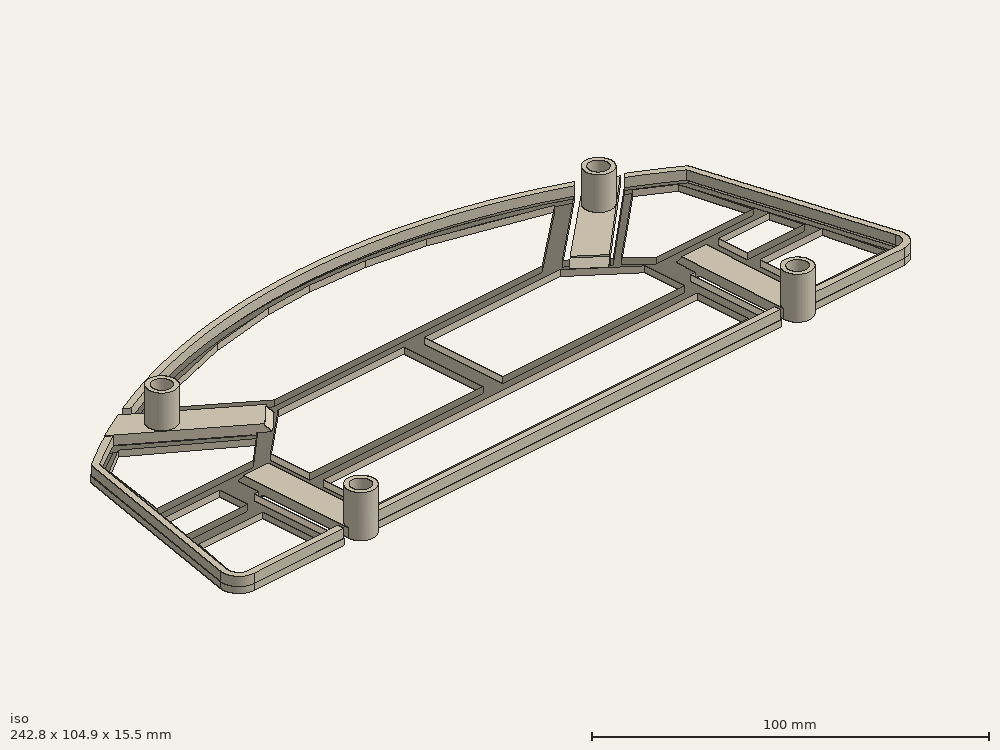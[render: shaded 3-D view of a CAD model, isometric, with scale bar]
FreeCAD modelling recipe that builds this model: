
FCSTD DOCUMENT  (FreeCAD 0.16R6045 (Git))
Label: project_n_rev3
License: All rights reserved
LicenseURL: http://en.wikipedia.org/wiki/All_rights_reserved
objects: Part::Cylinder×8, Sketcher::SketchObject×5, Part::Cut×5, Part::MultiFuse×4, Part::Chamfer×4, PartDesign::Pad×2, Part::Extrusion×2, Part::Thickness×1
note: 33 computed .brp shape members not serialized (recipe doc carries the construction recipe); baked Part::Feature solids carry a one-line shape summary decoded from their .brp

FEATURE [Sketcher::SketchObject] Sketch  label="Base"
  Placement = pos=(0,0,0) rot=(1,0,0;3.14159rad)
  sketch-geometry (71):
    g0: LineSegment StartX=-43.3507 StartY=-6.8712 StartZ=0 EndX=-28.7131 EndY=-67.7959 EndZ=0
    g1: LineSegment StartX=199.163 StartY=-6.8694 StartZ=0 EndX=184.746 EndY=-68.0609 EndZ=0
    g2: ArcOfCircle CenterX=-37.936 CenterY=-5.56776 CenterZ=0 NormalX=0 NormalY=0 NormalZ=1 Radius=5.56941 StartAngle=1.57075 EndAngle=3.37782
    g3: ArcOfCircle CenterX=193.736 CenterY=-5.5753 CenterZ=0 NormalX=0 NormalY=0 NormalZ=1 Radius=5.57903 StartAngle=6.0491 EndAngle=7.85398
    g4: ArcOfCircle CenterX=78.2135 CenterY=90.7587 CenterZ=0 NormalX=0 NormalY=0 NormalZ=1 Radius=191.24 StartAngle=4.11906 EndAngle=4.197
    g5: LineSegment StartX=-6 StartY=-32 StartZ=0 EndX=-6 EndY=0.000261594 EndZ=0
    g6: LineSegment StartX=6 StartY=-32 StartZ=0 EndX=6 EndY=0.000143702 EndZ=0
    g7: LineSegment StartX=-6 StartY=0.000261594 StartZ=0 EndX=-37.9357 EndY=0.00165396 EndZ=0
    g8: LineSegment StartX=150 StartY=-32.3968 StartZ=0 EndX=150 EndY=0.00359255 EndZ=0
    g9: LineSegment StartX=162 StartY=-32.3968 StartZ=0 EndX=161.882 EndY=0.00373137 EndZ=0
    g10: LineSegment StartX=150 StartY=0.00359255 StartZ=0 EndX=6 EndY=0.000143702 EndZ=0
    g11: LineSegment StartX=161.882 StartY=0.00373137 StartZ=0 EndX=193.736 EndY=0.00373137 EndZ=0
    g12: LineSegment StartX=-16.0434 StartY=-75.64 StartZ=0 EndX=15.3131 EndY=-52.4765 EndZ=0
    g13: LineSegment StartX=24.5337 StartY=-61.2587 StartZ=0 EndX=-3.03647 EndY=-82.3636 EndZ=0
    g14: ArcOfCircle CenterX=78.2135 CenterY=90.7587 CenterZ=0 NormalX=0 NormalY=0 NormalZ=1 Radius=191.24 StartAngle=4.27358 EndAngle=5.14801
    g15: LineSegment StartX=142 StartY=-52 StartZ=0 EndX=170.76 EndY=-76.5975 EndZ=0
    g16: LineSegment StartX=132.274 StartY=-60.4558 StartZ=0 EndX=158.911 EndY=-82.6217 EndZ=0
    g17: ArcOfCircle CenterX=78.2135 CenterY=90.7587 CenterZ=0 NormalX=0 NormalY=0 NormalZ=1 Radius=191.24 StartAngle=5.21752 EndAngle=5.30323
    g18: LineSegment StartX=5 StartY=-81.3932 StartZ=0 EndX=40.6717 EndY=-92 EndZ=0
    g19: LineSegment StartX=40.6717 StartY=-92 StartZ=0 EndX=62.6408 EndY=-95.7307 EndZ=0
    g20: LineSegment StartX=115.422 StartY=-92.1981 StartZ=0 EndX=150.549 EndY=-81.3932 EndZ=0
    g21: LineSegment StartX=150.549 StartY=-81.3932 StartZ=0 EndX=126.643 EndY=-62 EndZ=0
    g22: LineSegment StartX=126.643 StartY=-62 StartZ=0 EndX=31 EndY=-62 EndZ=0
    g23: LineSegment StartX=31 StartY=-62 StartZ=0 EndX=5 EndY=-81.3932 EndZ=0
    g24: LineSegment StartX=-10.9002 StartY=-29.4912 StartZ=0 EndX=-10.9002 EndY=-39.436 EndZ=0
    g25: LineSegment StartX=-10.9002 StartY=-39.436 StartZ=0 EndX=-30.4522 EndY=-39.436 EndZ=0
    g26: LineSegment StartX=-30.4522 StartY=-39.436 StartZ=0 EndX=-33 EndY=-29.4912 EndZ=0
    g27: LineSegment StartX=-33 StartY=-29.4912 StartZ=0 EndX=-10.9002 EndY=-29.4912 EndZ=0
    g28: LineSegment StartX=-10.9743 StartY=-5 StartZ=0 EndX=-10.9743 EndY=-24 EndZ=0
    g29: LineSegment StartX=-10.9743 StartY=-24 StartZ=0 EndX=-34 EndY=-24 EndZ=0
    g30: LineSegment StartX=-34 StartY=-24 StartZ=0 EndX=-39.0271 EndY=-5 EndZ=0
    g31: LineSegment StartX=-39.0271 StartY=-5 StartZ=0 EndX=-10.9743 EndY=-5 EndZ=0
    g32: LineSegment StartX=11.261 StartY=-6.50449 StartZ=0 EndX=11.261 EndY=-24.5558 EndZ=0
    g33: LineSegment StartX=11.261 StartY=-24.5558 StartZ=0 EndX=144.695 EndY=-24.5558 EndZ=0
    g34: LineSegment StartX=144.695 StartY=-24.5558 StartZ=0 EndX=144.695 EndY=-6.50449 EndZ=0
    g35: LineSegment StartX=144.695 StartY=-6.50449 StartZ=0 EndX=11.261 EndY=-6.50449 EndZ=0
    g36: LineSegment StartX=167.644 StartY=-25.2876 StartZ=0 EndX=190 EndY=-25.2876 EndZ=0
    g37: LineSegment StartX=190 StartY=-25.2876 StartZ=0 EndX=193.482 EndY=-6.26056 EndZ=0
    g38: LineSegment StartX=193.482 StartY=-6.26056 StartZ=0 EndX=167.644 EndY=-6.26056 EndZ=0
    g39: LineSegment StartX=167.644 StartY=-6.26056 StartZ=0 EndX=167.644 EndY=-25.2876 EndZ=0
    g40: LineSegment StartX=167.848 StartY=-40.4117 StartZ=0 EndX=186 EndY=-40.4117 EndZ=0
    g41: LineSegment StartX=186 StartY=-40.4117 StartZ=0 EndX=188.115 EndY=-29.9242 EndZ=0
    g42: LineSegment StartX=188.115 StartY=-29.9242 StartZ=0 EndX=167.848 EndY=-29.9242 EndZ=0
    g43: LineSegment StartX=167.848 StartY=-29.9242 StartZ=0 EndX=167.848 EndY=-40.4117 EndZ=0
    g44: LineSegment StartX=-28.746 StartY=-44 StartZ=0 EndX=-24 EndY=-65.8046 EndZ=0
    g45: LineSegment StartX=-24 StartY=-65.8046 StartZ=0 EndX=-14.6261 EndY=-71.8385 EndZ=0
    g46: LineSegment StartX=-14.6261 StartY=-71.8385 StartZ=0 EndX=14 EndY=-51.3805 EndZ=0
    g47: LineSegment StartX=14 StartY=-51.3805 StartZ=0 EndX=5.55797 EndY=-44 EndZ=0
    g48: LineSegment StartX=5.55797 StartY=-44 StartZ=0 EndX=-28.746 EndY=-44 EndZ=0
    g49: LineSegment StartX=184.574 StartY=-44.6904 StartZ=0 EndX=150 EndY=-44.6904 EndZ=0
    g50: LineSegment StartX=150 StartY=-44.6904 StartZ=0 EndX=143.578 EndY=-50.7188 EndZ=0
    g51: LineSegment StartX=143.578 StartY=-50.7188 StartZ=0 EndX=170 EndY=-73 EndZ=0
    g52: LineSegment StartX=170 StartY=-73 StartZ=0 EndX=180 EndY=-66.7707 EndZ=0
    g53: LineSegment StartX=180 StartY=-66.7707 StartZ=0 EndX=184.574 EndY=-44.6904 EndZ=0
    g54: LineSegment StartX=73 StartY=-29.4733 StartZ=0 EndX=73 EndY=-57.6014 EndZ=0
    g55: LineSegment StartX=73 StartY=-57.6014 StartZ=0 EndX=28 EndY=-57.6014 EndZ=0
    g56: LineSegment StartX=28 StartY=-57.6014 StartZ=0 EndX=11.2554 EndY=-43.539 EndZ=0
    g57: LineSegment StartX=11.2554 StartY=-43.539 StartZ=0 EndX=11.2554 EndY=-29.4733 EndZ=0
    g58: LineSegment StartX=11.2554 StartY=-29.4733 StartZ=0 EndX=73 EndY=-29.4733 EndZ=0
    g59: LineSegment StartX=80.0378 StartY=-29.4766 StartZ=0 EndX=80.0378 EndY=-57.4378 EndZ=0
    g60: LineSegment StartX=80.0378 StartY=-57.4378 StartZ=0 EndX=128.477 EndY=-57.4378 EndZ=0
    g61: LineSegment StartX=128.477 StartY=-57.4378 StartZ=0 EndX=145 EndY=-43.7025 EndZ=0
    g62: LineSegment StartX=145 StartY=-43.7025 StartZ=0 EndX=145 EndY=-29.4766 EndZ=0
    g63: LineSegment StartX=145 StartY=-29.4766 StartZ=0 EndX=80.0378 EndY=-29.4766 EndZ=0
    g64: LineSegment StartX=62.6408 StartY=-95.7307 StartZ=0 EndX=78 EndY=-96.5296 EndZ=0
    g65: LineSegment StartX=78 StartY=-96.5296 StartZ=0 EndX=97 EndY=-95.3313 EndZ=0
    g66: LineSegment StartX=97 StartY=-95.3313 StartZ=0 EndX=115.422 EndY=-92.1981 EndZ=0
    g67: LineSegment StartX=-6 StartY=-32 StartZ=0 EndX=6 EndY=-32 EndZ=0
    g68: LineSegment StartX=150 StartY=-32.3968 StartZ=0 EndX=162 EndY=-32.3968 EndZ=0
    g69: LineSegment StartX=15.3131 StartY=-52.4765 StartZ=0 EndX=24.5337 EndY=-61.2587 EndZ=0
    g70: LineSegment StartX=132.274 StartY=-60.4558 StartZ=0 EndX=142 EndY=-52 EndZ=0
  constraints (100):
    c: Coincident(g4,g0)
    c: Coincident(g17,g1)
    c: PointOnObject(g13,g4)
    c: Coincident(g4,g12)
    c: PointOnObject(g15,g14)
    c: Coincident(g14,g16)
    c: Coincident(g6,g10)
    c: Coincident(g9,g11)
    c: Coincident(g5,g7)
    c: Coincident(g10,g8)
    c: Coincident(g13,g14)
    c: Coincident(g15,g17)
    c: Coincident(g0,g2)
    c: Coincident(g3,g1)
    c: Coincident(g2,g7)
    c: Coincident(g3,g11)
    c: Coincident(g18,g19)
    c: Coincident(g66,g20)
    c: Coincident(g20,g21)
    c: Coincident(g21,g22)
    c: Horizontal(g22)
    c: Coincident(g22,g23)
    c: Coincident(g23,g18)
    c: Vertical(g24)
    c: Coincident(g24,g25)
    c: Horizontal(g25)
    c: Coincident(g25,g26)
    c: Coincident(g26,g27)
    c: Coincident(g27,g24)
    c: Horizontal(g27)
    c: Vertical(g28)
    c: Coincident(g28,g29)
    c: Horizontal(g29)
    c: Coincident(g29,g30)
    c: Coincident(g31,g30)
    c: Coincident(g31,g28)
    c: Horizontal(g31)
    c: Vertical(g32)
    c: Coincident(g32,g33)
    c: Horizontal(g33)
    c: Coincident(g33,g34)
    c: Vertical(g34)
    c: Coincident(g34,g35)
    c: Coincident(g35,g32)
    c: Horizontal(g35)
    c: Horizontal(g36)
    c: Coincident(g36,g37)
    c: Coincident(g37,g38)
    c: Horizontal(g38)
    c: Coincident(g38,g39)
    c: Coincident(g39,g36)
    c: Vertical(g39)
    c: Horizontal(g40)
    c: Coincident(g40,g41)
    c: Coincident(g41,g42)
    c: Horizontal(g42)
    c: Coincident(g42,g43)
    c: Coincident(g43,g40)
    c: Vertical(g43)
    c: Coincident(g44,g45)
    c: Coincident(g45,g46)
    c: Coincident(g46,g47)
    c: Coincident(g48,g47)
    c: Coincident(g48,g44)
    c: Horizontal(g48)
    c: Horizontal(g49)
    c: Coincident(g49,g50)
    c: Coincident(g50,g51)
    c: Coincident(g51,g52)
    c: Coincident(g52,g53)
    c: Coincident(g53,g49)
    c: Vertical(g54)
    c: Coincident(g54,g55)
    c: Horizontal(g55)
    c: Coincident(g55,g56)
    c: Coincident(g56,g57)
    c: Vertical(g57)
    c: Coincident(g57,g58)
    c: Coincident(g58,g54)
    c: Horizontal(g58)
    c: Vertical(g59)
    c: Coincident(g59,g60)
    c: Horizontal(g60)
    c: Coincident(g60,g61)
    c: Coincident(g61,g62)
    c: Vertical(g62)
    c: Coincident(g62,g63)
    c: Coincident(g63,g59)
    c: Horizontal(g63)
    c: Coincident(g64,g65)
    c: Coincident(g19,g64)
    c: Coincident(g66,g65)
    c: Coincident(g67,g5)
    c: Coincident(g67,g6)
    c: Horizontal(g67)
    c: Coincident(g68,g8)
    c: Coincident(g68,g9)
    c: Horizontal(g68)
    c: Coincident(g70,g16)
    c: Coincident(g70,g15)
FEATURE [Sketcher::SketchObject] Sketch004  label="Wall"
  sketch-geometry (29):
    g0: ArcOfCircle CenterX=78.2135 CenterY=90.7587 CenterZ=0 NormalX=0 NormalY=0 NormalZ=1 Radius=191.194 StartAngle=4.13378 EndAngle=4.19443
    g1: LineSegment StartX=-6 StartY=0 StartZ=0 EndX=-38 EndY=0 EndZ=0
    g2: LineSegment StartX=150 StartY=0 StartZ=0 EndX=5.75606 EndY=0 EndZ=0
    g3: LineSegment StartX=162 StartY=0 StartZ=0 EndX=193.736 EndY=0 EndZ=0
    g4: ArcOfCircle CenterX=78.3526 CenterY=90.8251 CenterZ=0 NormalX=0 NormalY=0 NormalZ=1 Radius=191.182 StartAngle=4.31861 EndAngle=5.10486
    g5: ArcOfCircle CenterX=78.2135 CenterY=90.7587 CenterZ=0 NormalX=0 NormalY=0 NormalZ=1 Radius=190.959 StartAngle=5.22699 EndAngle=5.28539
    g6: LineSegment StartX=5 StartY=-83 StartZ=0 EndX=39.505 EndY=-94 EndZ=0
    g7: LineSegment StartX=39.505 StartY=-94 StartZ=0 EndX=62.585 EndY=-98 EndZ=0
    g8: LineSegment StartX=115.781 StartY=-94.1981 StartZ=0 EndX=151.474 EndY=-83.5973 EndZ=0
    g9: LineSegment StartX=-38 StartY=-3.39482 StartZ=0 EndX=-6 EndY=-3.39482 EndZ=0
    g10: LineSegment StartX=149.756 StartY=-3.59354 StartZ=0 EndX=5.75606 EndY=-3.59354 EndZ=0
    g11: LineSegment StartX=193.736 StartY=-4.18044 StartZ=0 EndX=162 EndY=-4.18044 EndZ=0
    g12: LineSegment StartX=-24.7851 StartY=-67 StartZ=0 EndX=-14.3428 EndY=-73.6141 EndZ=0
    g13: LineSegment StartX=171 StartY=-74 StartZ=0 EndX=181 EndY=-67.7707 EndZ=0
    g14: LineSegment StartX=62.585 StartY=-98 StartZ=0 EndX=78 EndY=-98.5838 EndZ=0
    g15: LineSegment StartX=78 StartY=-98.5838 StartZ=0 EndX=97.359 EndY=-97.3313 EndZ=0
    g16: LineSegment StartX=97.359 StartY=-97.3313 StartZ=0 EndX=115.781 EndY=-94.1981 EndZ=0
    g17: LineSegment StartX=-6 StartY=0 StartZ=0 EndX=-6 EndY=-3.39482 EndZ=0
    g18: LineSegment StartX=5.75606 StartY=-3.59354 StartZ=0 EndX=5.75606 EndY=0 EndZ=0
    g19: LineSegment StartX=-38 StartY=0 StartZ=0 EndX=-38 EndY=-3.39482 EndZ=0
    g20: LineSegment StartX=150 StartY=0 StartZ=0 EndX=149.756 EndY=-3.59354 EndZ=0
    g21: LineSegment StartX=162 StartY=0 StartZ=0 EndX=162 EndY=-4.18044 EndZ=0
    g22: LineSegment StartX=193.736 StartY=0 StartZ=0 EndX=193.736 EndY=-4.18044 EndZ=0
    g23: LineSegment StartX=5 StartY=-83 StartZ=0 EndX=5 EndY=-85.7248 EndZ=0
    g24: LineSegment StartX=151.474 StartY=-83.5973 StartZ=0 EndX=151.474 EndY=-85.8208 EndZ=0
    g25: LineSegment StartX=171 StartY=-74 StartZ=0 EndX=172.201 EndY=-75.469 EndZ=0
    g26: LineSegment StartX=181 StartY=-67.7707 StartZ=0 EndX=181.744 EndY=-69.6997 EndZ=0
    g27: LineSegment StartX=-14.3428 StartY=-73.6141 StartZ=0 EndX=-16.4482 EndY=-75.3566 EndZ=0
    g28: LineSegment StartX=-24.7851 StartY=-67 StartZ=0 EndX=-26.3433 EndY=-69.3132 EndZ=0
  constraints (39):
    c: Coincident(g6,g7)
    c: Coincident(g16,g8)
    c: Horizontal(g9)
    c: Horizontal(g10)
    c: Horizontal(g11)
    c: Coincident(g14,g15)
    c: Coincident(g7,g14)
    c: Coincident(g16,g15)
    c: Coincident(g17,g1)
    c: Coincident(g17,g9)
    c: Vertical(g17)
    c: Coincident(g18,g10)
    c: Coincident(g18,g2)
    c: Vertical(g18)
    c: Coincident(g19,g1)
    c: Coincident(g19,g9)
    c: Vertical(g19)
    c: Coincident(g20,g2)
    c: Coincident(g20,g10)
    c: Coincident(g21,g3)
    c: Coincident(g21,g11)
    c: Vertical(g21)
    c: Coincident(g22,g3)
    c: Coincident(g22,g11)
    c: Vertical(g22)
    c: Coincident(g23,g6)
    c: Coincident(g23,g4)
    c: Vertical(g23)
    c: Coincident(g24,g8)
    c: Coincident(g24,g4)
    c: Vertical(g24)
    c: Coincident(g25,g13)
    c: Coincident(g25,g5)
    c: Coincident(g26,g13)
    c: Coincident(g26,g5)
    c: Coincident(g27,g12)
    c: Coincident(g27,g0)
    c: Coincident(g28,g12)
    c: Coincident(g28,g0)
FEATURE [Sketcher::SketchObject] Sketch006
  Placement = pos=(0,0,0) rot=(1,0,0;3.14159rad)
  sketch-geometry (10):
    g0: LineSegment StartX=-43.3507 StartY=-6.8712 StartZ=0 EndX=-28.6056 EndY=-67.6363 EndZ=0
    g1: LineSegment StartX=199.163 StartY=-6.8694 StartZ=0 EndX=184.746 EndY=-68.0609 EndZ=0
    g2: ArcOfCircle CenterX=-37.936 CenterY=-5.56776 CenterZ=0 NormalX=0 NormalY=0 NormalZ=1 Radius=5.56941 StartAngle=1.57075 EndAngle=3.37782
    g3: ArcOfCircle CenterX=193.736 CenterY=-5.5753 CenterZ=0 NormalX=0 NormalY=0 NormalZ=1 Radius=5.57903 StartAngle=6.0491 EndAngle=7.85398
    g4: ArcOfCircle CenterX=78.6813 CenterY=91.7773 CenterZ=0 NormalX=0 NormalY=0 NormalZ=1 Radius=192.154 StartAngle=4.12001 EndAngle=4.26651
    g5: LineSegment StartX=6 StartY=-0.234337 StartZ=0 EndX=-37.9357 EndY=0.00165396 EndZ=0
    g6: LineSegment StartX=161.599 StartY=-0.204933 StartZ=0 EndX=6 EndY=-0.234337 EndZ=0
    g7: LineSegment StartX=161.599 StartY=-0.204933 StartZ=0 EndX=193.736 EndY=0.00373137 EndZ=0
    g8: ArcOfCircle CenterX=78.463 CenterY=91.7918 CenterZ=0 NormalX=0 NormalY=0 NormalZ=1 Radius=192.073 StartAngle=4.26756 EndAngle=5.14419
    g9: ArcOfCircle CenterX=78.2123 CenterY=90.7613 CenterZ=0 NormalX=0 NormalY=0 NormalZ=1 Radius=191.243 StartAngle=5.14763 EndAngle=5.30323
  constraints (10):
    c: Coincident(g4,g0)
    c: Coincident(g9,g1)
    c: Coincident(g0,g2)
    c: Coincident(g3,g1)
    c: Coincident(g2,g5)
    c: Coincident(g3,g7)
    c: Coincident(g5,g6)
    c: Coincident(g6,g7)
    c: Coincident(g8,g9)
    c: Coincident(g4,g8)
FEATURE [PartDesign::Pad] Pad
  Length = 5
  Length2 = 100
  Placement = pos=(0,0,0) rot=(1,0,0;3.14159rad)
  Reversed = true
  Sketch = -> Sketch006
  Type = 0
FEATURE [Part::Thickness] Thickness
  Faces = -> Pad [Face11,Face12]
  Intersection = false
  Join = 0
  Mode = 1
  SelfIntersection = false
  Value = -2
FEATURE [Part::Extrusion] Extrude
  Base = -> Sketch
  Dir = (0,0,2)
  Solid = true
FEATURE [Part::Cylinder] Cylinder
  Angle = 360
  Height = 14
  Placement = pos=(0,0,1.5) rot=(0,0,1;0rad)
  Radius = 4.4
FEATURE [Part::Cylinder] Cylinder004
  Angle = 360
  Height = 12
  Placement = pos=(0,0,3.5) rot=(0,0,1;0rad)
  Radius = 3
FEATURE [Part::Cylinder] Cylinder001
  Angle = 360
  Height = 14
  Placement = pos=(155.8,0,1.5) rot=(0,0,1;0rad)
  Radius = 4.4
FEATURE [Part::Cylinder] Cylinder005
  Angle = 360
  Height = 12
  Placement = pos=(155.8,0,3.5) rot=(0,0,1;0rad)
  Radius = 3
FEATURE [Part::Cylinder] Cylinder002
  Angle = 360
  Height = 14
  Placement = pos=(155.8,71,1.5) rot=(0,0,1;0rad)
  Radius = 4.4
FEATURE [Part::Cylinder] Cylinder006
  Angle = 360
  Height = 12
  Placement = pos=(155.8,71,3.5) rot=(0,0,1;0rad)
  Radius = 3
FEATURE [Part::Cylinder] Cylinder003
  Angle = 360
  Height = 14
  Placement = pos=(0,71,1.5) rot=(0,0,1;0rad)
  Radius = 4.4
FEATURE [Part::Cylinder] Cylinder007
  Angle = 360
  Height = 12
  Placement = pos=(0,71,3.5) rot=(0,0,1;0rad)
  Radius = 3
FEATURE [Sketcher::SketchObject] Sketch007  label="Springy thing"
  Placement = pos=(0,0,1.5) rot=(1,0,0;3.14159rad)
  sketch-geometry (16):
    g0: LineSegment StartX=-4.40208 StartY=0 StartZ=0 EndX=-4.40208 EndY=-37.5004 EndZ=0
    g1: LineSegment StartX=4.40547 StartY=0 StartZ=0 EndX=4.40547 EndY=-37.5004 EndZ=0
    g2: LineSegment StartX=151.442 StartY=0 StartZ=0 EndX=151.761 EndY=-37.3467 EndZ=0
    g3: LineSegment StartX=160.216 StartY=0 StartZ=0 EndX=160.535 EndY=-37.3467 EndZ=0
    g4: LineSegment StartX=-15 StartY=-76.3521 StartZ=0 EndX=17.8292 EndY=-52.1593 EndZ=0
    g5: LineSegment StartX=-5.23652 StartY=-81.4351 StartZ=0 EndX=24.952 EndY=-58.8018 EndZ=0
    g6: ArcOfCircle CenterX=78.1816 CenterY=90.7137 CenterZ=0 NormalX=0 NormalY=0 NormalZ=1 Radius=191.295 StartAngle=4.20361 EndAngle=4.26116
    g7: LineSegment StartX=169.644 StartY=-77.1363 StartZ=0 EndX=139.631 EndY=-51 EndZ=0
    g8: LineSegment StartX=161 StartY=-81.5613 StartZ=0 EndX=132 EndY=-57.3864 EndZ=0
    g9: ArcOfCircle CenterX=78.2183 CenterY=90.7977 CenterZ=0 NormalX=0 NormalY=0 NormalZ=1 Radius=191.208 StartAngle=5.16014 EndAngle=5.21093
    g10: LineSegment StartX=151.442 StartY=0 StartZ=0 EndX=160.216 EndY=0 EndZ=0
    g11: LineSegment StartX=-4.40208 StartY=0 StartZ=0 EndX=4.40547 EndY=0 EndZ=0
    g12: LineSegment StartX=-4.40208 StartY=-37.5004 StartZ=0 EndX=4.40547 EndY=-37.5004 EndZ=0
    g13: LineSegment StartX=17.8292 StartY=-52.1593 StartZ=0 EndX=24.952 EndY=-58.8018 EndZ=0
    g14: LineSegment StartX=139.631 StartY=-51 StartZ=0 EndX=132 EndY=-57.3864 EndZ=0
    g15: LineSegment StartX=151.761 StartY=-37.3467 StartZ=0 EndX=160.535 EndY=-37.3467 EndZ=0
  constraints (19):
    c: Coincident(g6,g4)
    c: Coincident(g9,g8)
    c: Coincident(g5,g6)
    c: Coincident(g7,g9)
    c: Coincident(g10,g2)
    c: Coincident(g10,g3)
    c: Coincident(g11,g0)
    c: Coincident(g11,g1)
    c: Horizontal(g11)
    c: Coincident(g12,g0)
    c: Coincident(g12,g1)
    c: Horizontal(g12)
    c: Coincident(g13,g4)
    c: Coincident(g13,g5)
    c: Coincident(g14,g7)
    c: Coincident(g14,g8)
    c: Coincident(g15,g2)
    c: Coincident(g15,g3)
    c: Horizontal(g15)
FEATURE [Part::Extrusion] Extrude001
  Base = -> Sketch007
  Dir = (0,0,3)
  Solid = true
FEATURE [Part::MultiFuse] Fusion
  Shapes = -> [Extrude,Extrude001]
FEATURE [Part::Chamfer] Chamfer
  Base = -> Fusion
  Edges = 1 edges r=2: [Edge97]
FEATURE [Part::Chamfer] Chamfer001
  Base = -> Chamfer
  Edges = 1 edges r=2: [Edge16]
FEATURE [Part::Chamfer] Chamfer002
  Base = -> Chamfer001
  Edges = 2 edges r=2: [Edge27,Edge42]
FEATURE [Part::Chamfer] Chamfer003
  Base = -> Chamfer002
  Edges = 4 edges r=1.4: [Edge106,Edge124,Edge150,Edge179]
FEATURE [Sketcher::SketchObject] Sketch011
  Placement = pos=(0,0,0) rot=(1,0,0;3.14159rad)
  sketch-geometry (17):
    g0: LineSegment StartX=-17 StartY=-77 StartZ=0 EndX=-16.2168 EndY=-75.7568 EndZ=0
    g1: LineSegment StartX=-16.2168 StartY=-75.7568 StartZ=0 EndX=-13.3538 EndY=-73.5849 EndZ=0
    g2: LineSegment StartX=-13.3538 StartY=-73.5849 StartZ=0 EndX=-0.371851 EndY=-80.4461 EndZ=0
    g3: LineSegment StartX=-0.371851 StartY=-80.4461 StartZ=0 EndX=-4.37011 EndY=-83.7039 EndZ=0
    g4: LineSegment StartX=-4.37011 StartY=-83.7039 StartZ=0 EndX=-17 EndY=-77 EndZ=0
    g5: LineSegment StartX=171.197 StartY=-77 StartZ=0 EndX=168.944 EndY=-75 EndZ=0
    g6: LineSegment StartX=168.944 StartY=-75 StartZ=0 EndX=157 EndY=-81 EndZ=0
    g7: LineSegment StartX=157 StartY=-81 StartZ=0 EndX=161 EndY=-84.5874 EndZ=0
    g8: LineSegment StartX=161 StartY=-84.5874 StartZ=0 EndX=171.197 EndY=-77 EndZ=0
    g9: LineSegment StartX=150 StartY=0.629851 StartZ=0 EndX=150 EndY=-3.46712 EndZ=0
    g10: LineSegment StartX=150 StartY=-3.46712 StartZ=0 EndX=162 EndY=-3.46712 EndZ=0
    g11: LineSegment StartX=162 StartY=-3.46712 StartZ=0 EndX=162 EndY=2.35749 EndZ=0
    g12: LineSegment StartX=162 StartY=2.35749 StartZ=0 EndX=150 EndY=0.629851 EndZ=0
    g13: LineSegment StartX=-6 StartY=1.22898 StartZ=0 EndX=-6 EndY=-5 EndZ=0
    g14: LineSegment StartX=-6 StartY=-5 StartZ=0 EndX=6 EndY=-5 EndZ=0
    g15: LineSegment StartX=6 StartY=-5 StartZ=0 EndX=6 EndY=2.75918 EndZ=0
    g16: LineSegment StartX=6 StartY=2.75918 StartZ=0 EndX=-6 EndY=1.22898 EndZ=0
  constraints (23):
    c: Coincident(g0,g1)
    c: Coincident(g1,g2)
    c: Coincident(g2,g3)
    c: Coincident(g3,g4)
    c: Coincident(g4,g0)
    c: Coincident(g5,g6)
    c: Coincident(g6,g7)
    c: Coincident(g7,g8)
    c: Coincident(g8,g5)
    c: Vertical(g9)
    c: Coincident(g9,g10)
    c: Horizontal(g10)
    c: Coincident(g10,g11)
    c: Vertical(g11)
    c: Coincident(g11,g12)
    c: Coincident(g12,g9)
    c: Vertical(g13)
    c: Coincident(g13,g14)
    c: Horizontal(g14)
    c: Coincident(g14,g15)
    c: Vertical(g15)
    c: Coincident(g15,g16)
    c: Coincident(g16,g13)
FEATURE [PartDesign::Pad] Pad001
  Length = 10
  Length2 = 100
  Placement = pos=(0,0,0) rot=(1,0,0;3.14159rad)
  Reversed = true
  Sketch = -> Sketch011
  Type = 0
FEATURE [Part::Cut] Cut
  Base = -> Thickness
  Tool = -> Pad001
FEATURE [Part::Cut] Cut001
  Base = -> Cylinder
  Tool = -> Cylinder004
FEATURE [Part::Cut] Cut002
  Base = -> Cylinder002
  Tool = -> Cylinder006
FEATURE [Part::Cut] Cut003
  Base = -> Cylinder003
  Tool = -> Cylinder007
FEATURE [Part::Cut] Cut004
  Base = -> Cylinder001
  Tool = -> Cylinder005
FEATURE [Part::MultiFuse] Fusion001  label="Legs"
  Shapes = -> [Cut001,Cut003,Cut004,Cut002]
FEATURE [Part::MultiFuse] Fusion002
  Shapes = -> [Cut,Chamfer003]
FEATURE [Part::MultiFuse] Fusion003
  Shapes = -> [Fusion001,Fusion002]
